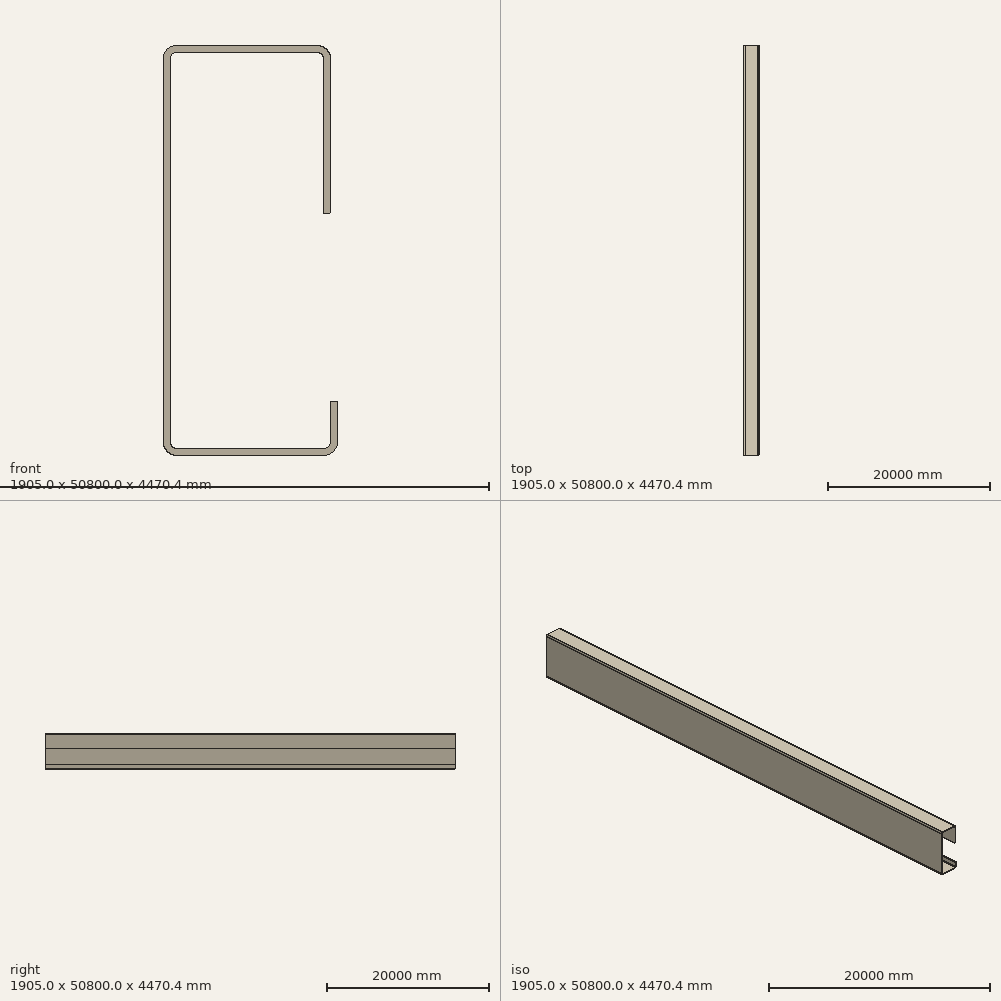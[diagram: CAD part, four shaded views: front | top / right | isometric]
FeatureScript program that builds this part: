
annotation { "Feature Type Name" : "Feature", "Feature Type Description" : "" }
export const myFeature = defineFeature(function(context is Context, id is Id, definition is map)
    precondition{}
    {
        {
            var Q0;
            Q0=qCreatedBy(makeId("Front.planeOp"),FACE);
            var sketch = newSketch(context, id + "F0", { "sketchPlane" : qUnion([Q0])});
            skLineSegment(sketch, "E0", {"start": v(1331.18, 373.41) * mm, "end": v(-192.82, 373.41) * mm});
            skArc(sketch, "E1", {"start": v(-192.82, 373.41) * mm, "mid": v(-246.7, 351.1) * mm, "end": v(-269.02, 297.21) * mm});
            skLineSegment(sketch, "E2", {"start": v(-269.02, 297.21) * mm, "end": v(-269.02, -3868.39) * mm});
            skArc(sketch, "E3", {"start": v(-269.02, -3868.39) * mm, "mid": v(-246.7, -3922.27) * mm, "end": v(-192.82, -3944.59) * mm});
            skLineSegment(sketch, "E4", {"start": v(-192.82, -3944.59) * mm, "end": v(1407.38, -3944.59) * mm});
            skArc(sketch, "E5", {"start": v(1407.38, -3944.59) * mm, "mid": v(1461.26, -3922.27) * mm, "end": v(1483.58, -3868.39) * mm});
            skArc(sketch, "E6", {"start": v(1331.18, 373.41) * mm, "mid": v(1385.06, 351.1) * mm, "end": v(1407.38, 297.21) * mm});
            skLineSegment(sketch, "E7", {"start": v(1407.38, 297.21) * mm, "end": v(1407.38, -1379.19) * mm});
            skLineSegment(sketch, "E8", {"start": v(1483.58, -3868.39) * mm, "end": v(1483.58, -3436.59) * mm});
            skLineSegment(sketch, "E9.0", {"start": v(1483.58, 297.21) * mm, "end": v(1483.58, -1379.19) * mm});
            skArc(sketch, "E10.0", {"start": v(1331.18, 449.61) * mm, "mid": v(1438.94, 404.97) * mm, "end": v(1483.58, 297.21) * mm});
            skLineSegment(sketch, "E11.0", {"start": v(1483.58, 449.61) * mm, "end": v(-192.82, 449.61) * mm});
            skLineSegment(sketch, "E12.0", {"start": v(-192.82, 297.21) * mm, "end": v(-192.82, 297.21) * mm});
            skLineSegment(sketch, "E13.0", {"start": v(-345.22, 449.61) * mm, "end": v(-345.22, -3868.39) * mm});
            skArc(sketch, "E14.0", {"start": v(-192.82, 449.61) * mm, "mid": v(-300.59, 404.97) * mm, "end": v(-345.22, 297.21) * mm});
            skArc(sketch, "E15.0", {"start": v(-345.22, -3868.39) * mm, "mid": v(-300.59, -3976.15) * mm, "end": v(-192.82, -4020.79) * mm});
            skLineSegment(sketch, "E16.0", {"start": v(-192.82, -4020.79) * mm, "end": v(1559.78, -4020.79) * mm});
            skArc(sketch, "E17.0", {"start": v(1407.38, -4020.79) * mm, "mid": v(1515.14, -3976.15) * mm, "end": v(1559.78, -3868.39) * mm});
            skLineSegment(sketch, "E18.0", {"start": v(1559.78, -3868.39) * mm, "end": v(1559.78, -3436.59) * mm});
            skLineSegment(sketch, "E19", {"start": v(1559.78, -3436.59) * mm, "end": v(1483.58, -3436.59) * mm});
            skLineSegment(sketch, "E20", {"start": v(1407.38, -1379.19) * mm, "end": v(1483.58, -1379.19) * mm});
            skSolve(sketch);
        }
        {
            var Q0;
            Q0 = qSketchRegion(id + "F0", true);
            extrude(context, id + "F1", {"entities" : qUnion([Q0]), "depth" : 50800 * mm, "offsetDistance" : 25.4 * mm});
        }
    });
